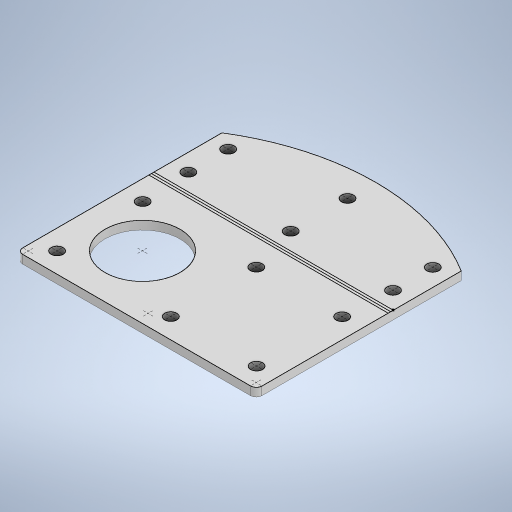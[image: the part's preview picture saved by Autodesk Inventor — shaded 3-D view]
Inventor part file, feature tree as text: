
AUTODESK INVENTOR PART (.ipt)
format: ipt  version: 2024.2 (Build 282272000, 272)  size: 278,016 bytes
history: native  units: in
note: dims shown in document units (in); Inventor stores cm internally (conversion verified against a paired STEP export)
features: sketch x1, extrude x1
ambient origin geometry x8: Origin, YZ Plane, XZ Plane, XY Plane, X Axis, Y Axis, Z Axis, Center Point
bodies: Solid1 (feature_tree)
feature tree (2):
  sketch  "Sketch1"  dims[d1=0.0591in d2=0.0in]
  extrude  "Extrusion1"  [1 undecoded]
note: 1 required parameter value undecoded (feature->parameter linkage not recoverable at this tier; creation-order binding heuristic only, values carry confidence <= 0.55)
